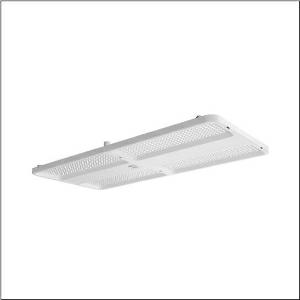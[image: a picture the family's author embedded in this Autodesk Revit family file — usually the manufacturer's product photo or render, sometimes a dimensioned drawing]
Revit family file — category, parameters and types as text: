
# Revit family: highbay_21_maxi_52hn11db4qda03
name_source: partatom
category: Lighting Fixtures
units: mm (PartAtom-declared; Revit-internal decimal feet)

## family parameters
Cut with Voids When Loaded = No
Host = Face
Light Source = No
Part Type = Normal
Room Calculation Point = No
Round Connector Dimension = Use Diameter
Shared = No

## types (1)
- --- (1 x LED, 38000 lm, 197.7 W, 4000K)
    Apparent Load = 198 VA
    CIE Flux Codes = 89 97 99 100 100
    Color Rendering = 80
    Color Temperature = 4000K
    Default Elevation = 1800 mm
    Description = high bay luminaire Highbay 21 maxi; direct symmetric narrow distribution, light control with lens of PMMA; UGR ≤ 19 (X = 4H | Y = 8H | S = 0.25H | reflection values 70/50/20); luminous flux: 38.000lm; light colour: 840, colour temperature: 4000K, MacAdam ≤ 3 SDCM (initial), colour rendering: CRI > 80; luminous efficacy: 192,2lm/W; rated service life: 75.000h (L80/B50) at AT= ta max; control: DALI 2; for wired networking: open and standardized DALI2 interface enables full flexibility and future-proofing for changes in use or functional adaptation through individual programming; multi-sensor luminaire consisting of a DALI2 multi-sensor and DALI2 ECG; multi-sensor luminaire for wired connection to a DALI2 application controller (e.g., SITECO Connect 11 or 21); can also be connected to existing on-site lighting or building automation systems upon request; integrated DALI2 sensor certified according to IEC 62386, Parts 101, 103, 303, and 304; integrated DALI2 ECG provides luminaire data (according to IEC 62386, Part 251), energy data (Part 252), and monitoring and analytics data (Part 253) to higher-level systems for further processing; luminaire with PIR sensor (passive-infrared); with light sensor; luminaire connection: terminal, 5-pole, max. 2.5mm² (cable entry for one cable, Ø 8.5..16mm); mains connection: 230..240V, AC 50/60Hz; connected load: 197,7W; protection rating (complete): IP65; insulation class (complete): insulation class I (protective earthing); protection symbol: D; certification: CE, ENEC, VDE, UKCA; internal wiring halogen-free; luminaire corresponds to IFS (International Featured Standards) requirements for safety and quality in the food industry; LABS conformity tested according to VDMA 24364:2018-05; housing frame of high-performance plastic PA6, matt traffic white (RAL 9016); cover of PMMA; dimension (LxWxH): 946 x 442 x 72mm; permissible operating ambient temperature: -20..+40°C (reducing of maximum allowable ambient temperature of 5°C with ceiling mounting); packaging unit: 1 piece; (delivery without accessories; please order mounting accessories separately)
    Height = 72 mm  [stored 0.23622 ft]
    Lamp = 1 x LED
    Lamp Light Flux = 38000 lm
    Lamp Power = 197.7 W
    Lamp count = 1
    Length = 946 mm
    Luminous efficacy = 192 lm/W
    Manufacturer = Siteco
    ModVariant = No
    Model = 52HN11DB4QDA03
    Mounting Place = Ceiling
    Mounting Type = Pendant
    Number of Poles = 1
    OnlyDefault = Yes
    Power Factor = 1
    Product Name = Highbay 21 maxi
    Product group = high bay luminaire
    ProductGroupID = 901
    Protection Class = Protection class I
    Protection Degree = IP 65
    RLX_Detail_Level = 1
    RLX_Emergency_Light_Flux = 0 lm
    RLX_Emergency_Type = 0
    RLX_Emergency_Type_DB = No
    RlxData = <blob elided: 128573 chars, md5=20c33cd0>
    Socket = socket
    Standby Power = 0 W
    System Light Flux = 38000 lm
    System Power = 198 W
    Type Comments = factory setting: luminous flux: 100 % | dim-lin: 254 | 918 mA
    Type Image = l_1363267.jpg
    URL = http://relux.com
    VarID = @adj_010023
    Voltage = 0 V
    Weight = 0.00 kg
    Width = 442 mm

note: [stored X ft] marks values corroborated as IEEE doubles in the binary element streams (Revit-internal decimal feet)

## geometry (parser evidence)
native form markers: Blend x4, Sweep x10
no freeform markers — native parametric forms only
